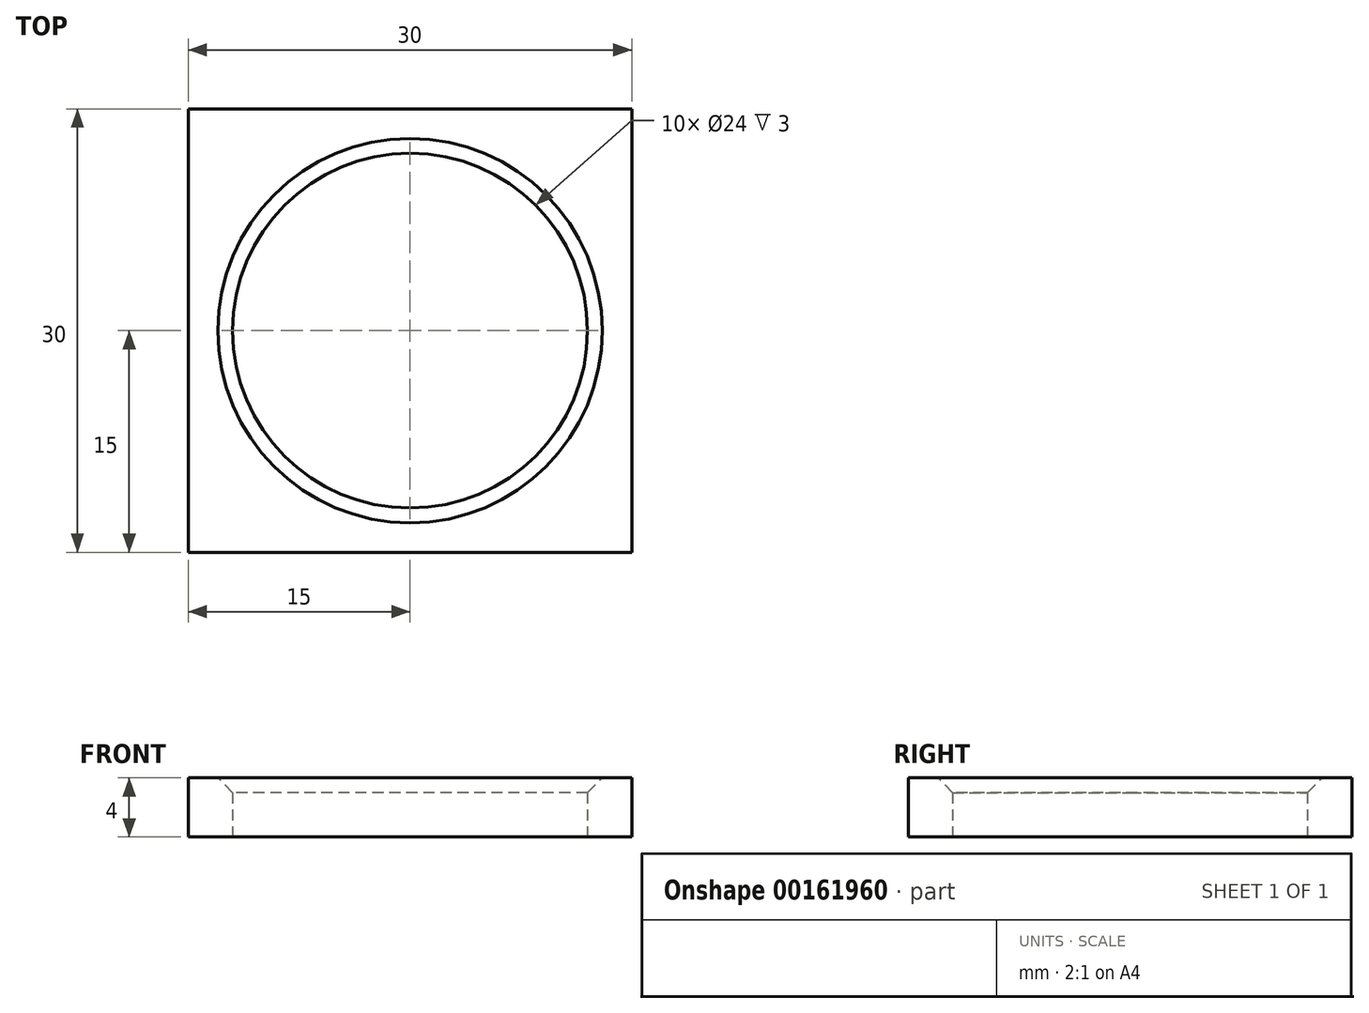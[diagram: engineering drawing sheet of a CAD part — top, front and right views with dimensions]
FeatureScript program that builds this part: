
annotation { "Feature Type Name" : "Feature", "Feature Type Description" : "" }
export const myFeature = defineFeature(function(context is Context, id is Id, definition is map)
    precondition{}
    {
        {
            var Q0;
            Q0=qCreatedBy(makeId("Top.planeOp"),FACE);
            var sketch = newSketch(context, id + "F0", { "sketchPlane" : qUnion([Q0])});
            skLineSegment(sketch, "E0.bottom", {"start": v(-15, 15) * mm, "end": v(15, 15) * mm});
            skLineSegment(sketch, "E0.top", {"start": v(-15, -15) * mm, "end": v(15, -15) * mm});
            skLineSegment(sketch, "E0.left", {"start": v(-15, 15) * mm, "end": v(-15, -15) * mm});
            skLineSegment(sketch, "E0.right", {"start": v(15, 15) * mm, "end": v(15, -15) * mm});
            skPoint(sketch, "E0.middle", {"position": v(0, 0) * mm});
            skCircle(sketch, "E1", {"center": v(0, 0) * mm, "radius": 12 * mm});
            skSolve(sketch);
        }
        {
            var Q0;
            Q0 = qSketchRegion(id + "F0", true);
            extrude(context, id + "F1", {"entities" : qUnion([Q0]), "depth" : 4 * mm});
        }
        {
            var Q0;
            Q0=makeQuery(id+"F1.opExtrude","CAP_EDGE",EDGE,{"disambiguationData":[OSD([sQuery(id+"F0.wireOp",EDGE,"E1")])],"isStart":false});
            chamfer(context, id + "F2", {"entities" : qUnion([Q0]), "width" : 1 * mm, "tangentPropagation" : true});
        }
    });
